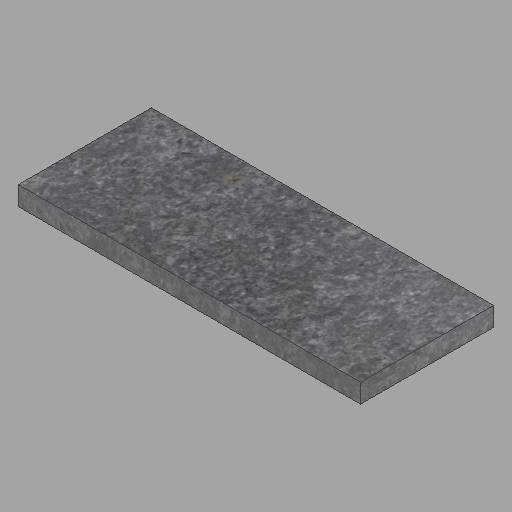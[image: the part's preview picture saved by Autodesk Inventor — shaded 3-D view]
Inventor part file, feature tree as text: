
AUTODESK INVENTOR PART (.ipt)
format: ipt  version: 2023 (Build 270158000, 158)  size: 221,696 bytes
history: native  units: in
note: dims shown in document units (in); Inventor stores cm internally (conversion verified against a paired STEP export)
features: other x1, extrude x1, sketch x1
ambient origin geometry x8: Origin, YZ Plane, XZ Plane, XY Plane, X Axis, Y Axis, Z Axis, Center Point
bodies: Solid1 (feature_tree)
feature tree (3):
  other  "2x14x36-15"
  extrude  "Extrusion1"  Depth=2.0in
  sketch  "Sketch1"  dims[d0=14.0in d1=2.0in d2=36.0in d3=0.0in]
